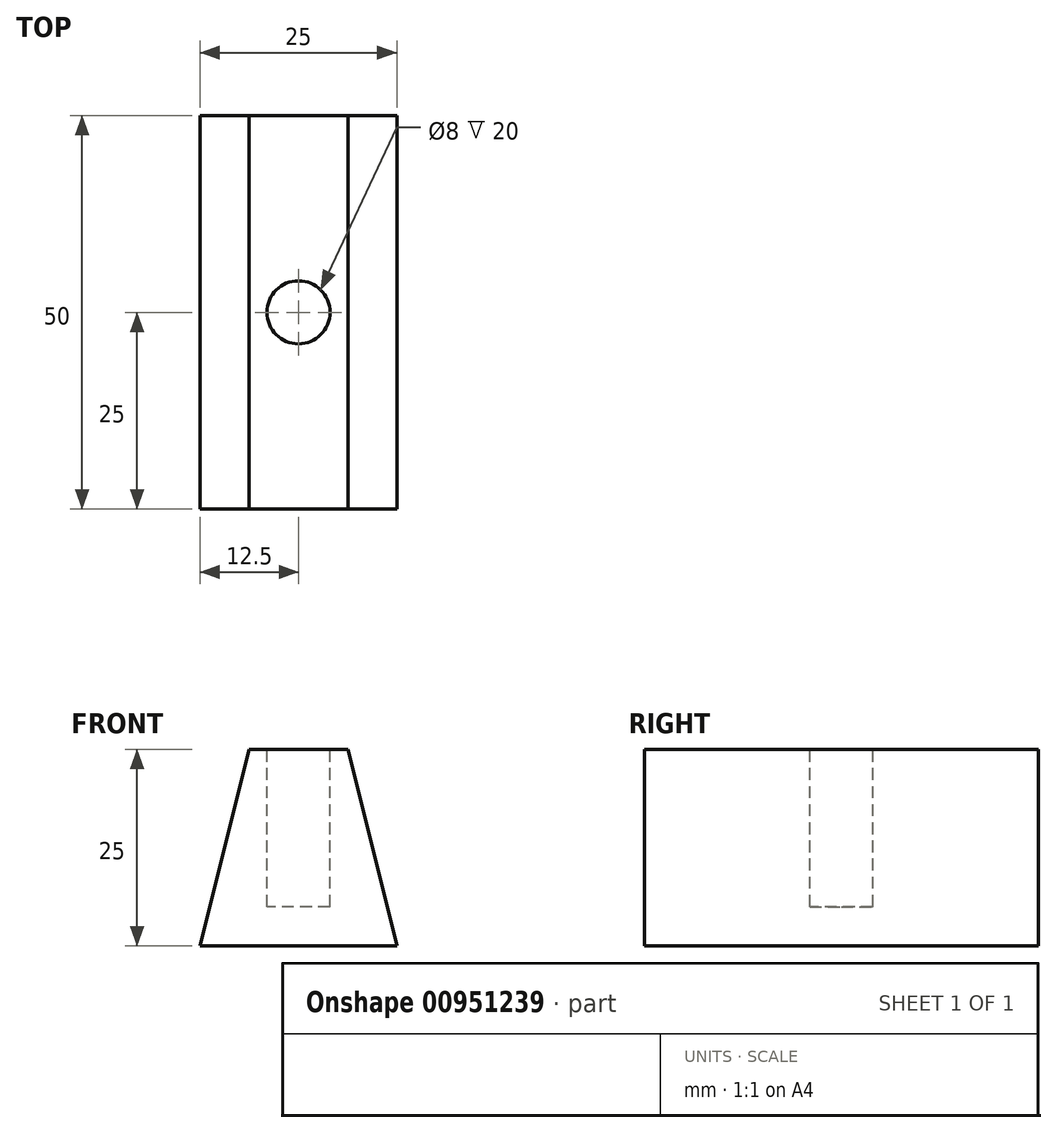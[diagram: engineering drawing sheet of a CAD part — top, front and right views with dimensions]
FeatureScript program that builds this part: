
annotation { "Feature Type Name" : "Feature", "Feature Type Description" : "" }
export const myFeature = defineFeature(function(context is Context, id is Id, definition is map)
    precondition{}
    {
        {
            var Q0;
            Q0=qCreatedBy(makeId("Front.planeOp"),FACE);
            var sketch = newSketch(context, id + "F0", { "sketchPlane" : qUnion([Q0])});
            skLineSegment(sketch, "E0", {"start": v(-12.5, 0) * mm, "end": v(12.5, 0) * mm});
            skLineSegment(sketch, "E1", {"start": v(12.5, 0) * mm, "end": v(6.27, 25) * mm});
            skLineSegment(sketch, "E2", {"start": v(6.27, 25) * mm, "end": v(-6.27, 25) * mm});
            skLineSegment(sketch, "E3", {"start": v(-6.27, 25) * mm, "end": v(-12.5, 0) * mm});
            skPoint(sketch, "E4", {"position": v(0, 0) * mm});
            skSolve(sketch);
        }
        {
            var Q0;
            Q0=makeQuery(id+"F0.imprint","IMPRINT",FACE,{"disambiguationData":[TD([[makeQuery(id+"F0.imprint","IMPRINT",EDGE,{"derivedFrom":sQuery(id+"F0.wireOp",EDGE,"E0")}),1.0]])]});
            extrude(context, id + "F1", {"entities" : qUnion([Q0]), "oppositeDirection" : true, "depth" : 50 * mm, "offsetDistance" : 25 * mm});
        }
        {
            var Q0;
            Q0=makeQuery(id+"F1.opExtrude","SWEPT_FACE",FACE,{"disambiguationData":[OSD([sQuery(id+"F0.wireOp",EDGE,"E2")])]});
            var sketch = newSketch(context, id + "F2", { "sketchPlane" : qUnion([Q0])});
            skCircle(sketch, "E5", {"center": v(0, 25) * mm, "radius": 4 * mm});
            skPoint(sketch, "E5.centerSnap0", {"position": v(-6.27, 25) * mm});
            skSolve(sketch);
        }
        {
            var Q0;
            Q0 = qSketchRegion(id + "F2", true);
            extrude(context, id + "F3", {"entities" : qUnion([Q0]), "operationType" : NewBodyOperationType.REMOVE, "oppositeDirection" : true, "depth" : 20 * mm, "offsetDistance" : 25 * mm});
        }
    });
